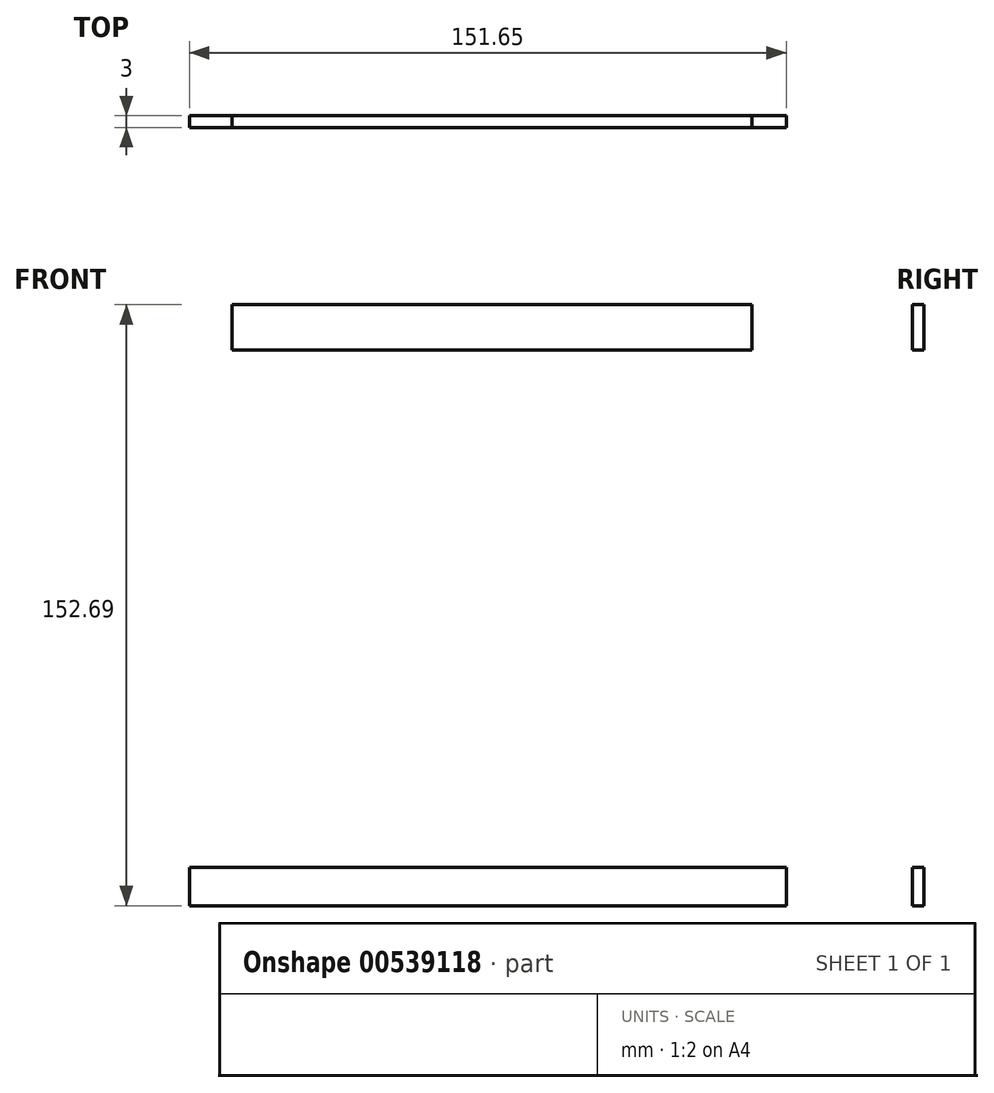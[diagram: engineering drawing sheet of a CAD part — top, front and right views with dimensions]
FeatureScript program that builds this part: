
annotation { "Feature Type Name" : "Feature", "Feature Type Description" : "" }
export const myFeature = defineFeature(function(context is Context, id is Id, definition is map)
    precondition{}
    {
        {
            var Q0;
            Q0=qCreatedBy(makeId("Front.planeOp"),FACE);
            var sketch = newSketch(context, id + "F0", { "sketchPlane" : qUnion([Q0])});
            skLineSegment(sketch, "E0.bottom", {"start": v(-75.72, -76.55) * mm, "end": v(75.93, -76.55) * mm});
            skLineSegment(sketch, "E0.top", {"start": v(-75.72, -66.8) * mm, "end": v(75.93, -66.8) * mm});
            skLineSegment(sketch, "E0.left", {"start": v(-75.72, -76.55) * mm, "end": v(-75.72, -66.8) * mm});
            skLineSegment(sketch, "E0.right", {"start": v(75.93, -76.55) * mm, "end": v(75.93, -66.8) * mm});
            skLineSegment(sketch, "E1.bottom", {"start": v(-75.72, -66.8) * mm, "end": v(-64.93, -66.8) * mm});
            skLineSegment(sketch, "E1.top", {"start": v(-75.72, 76.55) * mm, "end": v(-64.93, 76.55) * mm});
            skLineSegment(sketch, "E1.left", {"start": v(-75.72, -66.8) * mm, "end": v(-75.72, 76.55) * mm});
            skLineSegment(sketch, "E1.right", {"start": v(-64.93, -66.8) * mm, "end": v(-64.93, 76.55) * mm});
            skLineSegment(sketch, "E2.bottom", {"start": v(75.93, -66.8) * mm, "end": v(67.22, -66.8) * mm});
            skLineSegment(sketch, "E2.top", {"start": v(75.93, 76.14) * mm, "end": v(67.22, 76.14) * mm});
            skLineSegment(sketch, "E2.left", {"start": v(75.93, -66.8) * mm, "end": v(75.93, 76.14) * mm});
            skLineSegment(sketch, "E2.right", {"start": v(67.22, -66.8) * mm, "end": v(67.22, 76.14) * mm});
            skLineSegment(sketch, "E3.bottom", {"start": v(67.22, 76.14) * mm, "end": v(-64.93, 76.14) * mm});
            skLineSegment(sketch, "E3.top", {"start": v(67.22, 64.6) * mm, "end": v(-64.93, 64.6) * mm});
            skLineSegment(sketch, "E3.left", {"start": v(67.22, 76.14) * mm, "end": v(67.22, 64.6) * mm});
            skLineSegment(sketch, "E3.right", {"start": v(-64.93, 76.14) * mm, "end": v(-64.93, 64.6) * mm});
            skSolve(sketch);
        }
        {
            var Q0;
            Q0=makeQuery(id+"F0.imprint","IMPRINT",FACE,{"disambiguationData":[TD([[makeQuery(id+"F0.imprint","IMPRINT",EDGE,{"derivedFrom":sQuery(id+"F0.wireOp",EDGE,"E0.bottom")}),1.0]])]});
            var Q1;
            {var subQ1=sQuery(id+"F0.wireOp",EDGE,"E1.bottom");Q1=makeQuery(id+"F0.imprint","IMPRINT",FACE,{"disambiguationData":[TD([[makeQuery(id+"F0.imprint","IMPRINT",EDGE,{"derivedFrom":subQ1}),1.0]])]});}
            var Q2;
            Q2=makeQuery(id+"F0.imprint","IMPRINT",FACE,{"disambiguationData":[TD([[makeQuery(id+"F0.imprint","IMPRINT",EDGE,{"derivedFrom":sQuery(id+"F0.wireOp",EDGE,"E3.bottom")}),1.0]])]});
            var Q3;
            Q3=makeQuery(id+"F0.imprint","IMPRINT",FACE,{"disambiguationData":[TD([[makeQuery(id+"F0.imprint","IMPRINT",EDGE,{"derivedFrom":sQuery(id+"F0.wireOp",EDGE,"E2.bottom")}),-1.0]])]});
            extrude(context, id + "F1", {"entities" : qUnion([Q0, Q1, Q2, Q3]), "depth" : 3 * mm, "offsetDistance" : 25.4 * mm});
        }
    });
